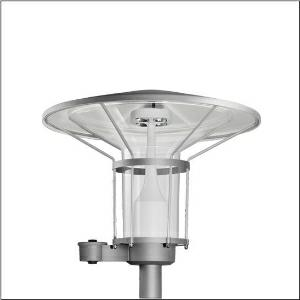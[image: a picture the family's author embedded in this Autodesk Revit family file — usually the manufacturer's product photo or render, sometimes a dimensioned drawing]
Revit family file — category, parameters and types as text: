
# Revit family: laterne_classic_iq___st1_2a_5xa5245ey14h000022_9375
name_source: partatom
category: Lighting Fixtures
units: mm (PartAtom-declared; Revit-internal decimal feet)

## family parameters
Cut with Voids When Loaded = No
Host = Face
Light Source = No
Part Type = Normal
Room Calculation Point = No
Round Connector Dimension = Use Diameter
Shared = No

## types (1)
- --- (1 x LED, 1370 lm, 10.7 W, 3000K)
    Apparent Load = 11 VA
    CIE Flux Codes = 21 60 93 97 100
    Color Rendering = 70
    Color Temperature = 3000K
    Default Elevation = 1800 mm
    Description = Lantern Classic iQ, mast luminaire, Module 540 iQ-SR, primary light control with 3 zone facetted reflector, of plastic, silver coated, highly specular, structured, primary optical cover: cover, of PMMA, transparent, light distribution: ST1.2a, light emission: direct distribution, primary light characteristic: asymmetric, installation type: post-top, LED, High Power LED, rated luminous flux: 1.370lm, luminous efficacy: 128lm/W, light colour: 730, colour temperature: 3000K, control gear: iQ-Street Remote, D4i with power reduction, control: optimised constant luminous flux control (CLO 2.0), Desk-Remote (wireless, voltage-free reading and setting of iQ features in the workshop via application-optimized NFC function/RFID function), Light-Fading, Smart-Wire, Night-Set, Lumen-Switch, Temp-Guard, Auto-Match, Street-Remote, pre-setting: logarithmic dimming characteristic, with terminal, 6-pole, max. 2.5mm², mains connection: 230..240V, AC, 50/60Hz, connection cable pre-assembled, cable length: 5,5m, wiring characteristics: H07RN-F, start of lifetime: 11W, end of service life: 11W, reduction: 6W, luminaire housing, upper part, of glass-fibre reinforced polyester, coated, Siteco® metallic grey (DB 702S), diameter: 750mm, height: 596mm, spigot size: d x l = 76 x 70mm (post-top) | with reducer (optional accessory) 60 x 70mm, mounting height: 3..5m, post-top mast mounting element, of diecast aluminium, coated, Siteco® metallic grey (DB 702S), Module 540 iQ-SR, traffic white (RAL 9016), equipment: standard, Smart Interface below and above, protection rating (complete): IP65, insulation class (complete): insulation class II (safety insulation), certification: CE, ENEC, VDE, packaging unit: 1 piece

Light Distribution: ST1.2a
    Height = 596 mm
    Lamp = 1 x LED
    Lamp Light Flux = 1370 lm
    Lamp Power = 10.7 W
    Lamp count = 1
    Length = 750 mm
    Luminous efficacy = 128 lm/W
    Manufacturer = Siteco
    ModVariant = No
    Model = 5XA5245EY14H000022
    Number of Poles = 1
    OnlyDefault = Yes
    Power Factor = 1
    Product Name = Laterne Classic iQ | ST1.2a
    Product group = mast luminaire | pylon top
    ProductGroupID = 6100
    Protection Class = Protection class II
    Protection Degree = IP 65
    RLX_Detail_Level = 1
    RLX_Emergency_Light_Flux = 0 lm
    RLX_Emergency_Type = 0
    RLX_Emergency_Type_DB = No
    RlxData = <blob elided: 63713 chars, md5=f9ad54de>
    Socket = socket
    Standby Power = 0 W
    System Light Flux = 1370 lm
    System Power = 11 W
    Type Comments = factory setting: luminous flux: 100 % | dim-lin: 254 | 419 mA
    Type Image = l_1006522.jpg
    URL = http://relux.com
    VarID = @adj_083828
    Voltage = 0 V
    Weight = 0.00 kg
    Width = 0 mm  [stored 0 ft]

note: [stored X ft] marks values corroborated as IEEE doubles in the binary element streams (Revit-internal decimal feet)

## geometry (parser evidence)
native form markers: Blend x4, Sweep x9
no freeform markers — native parametric forms only
